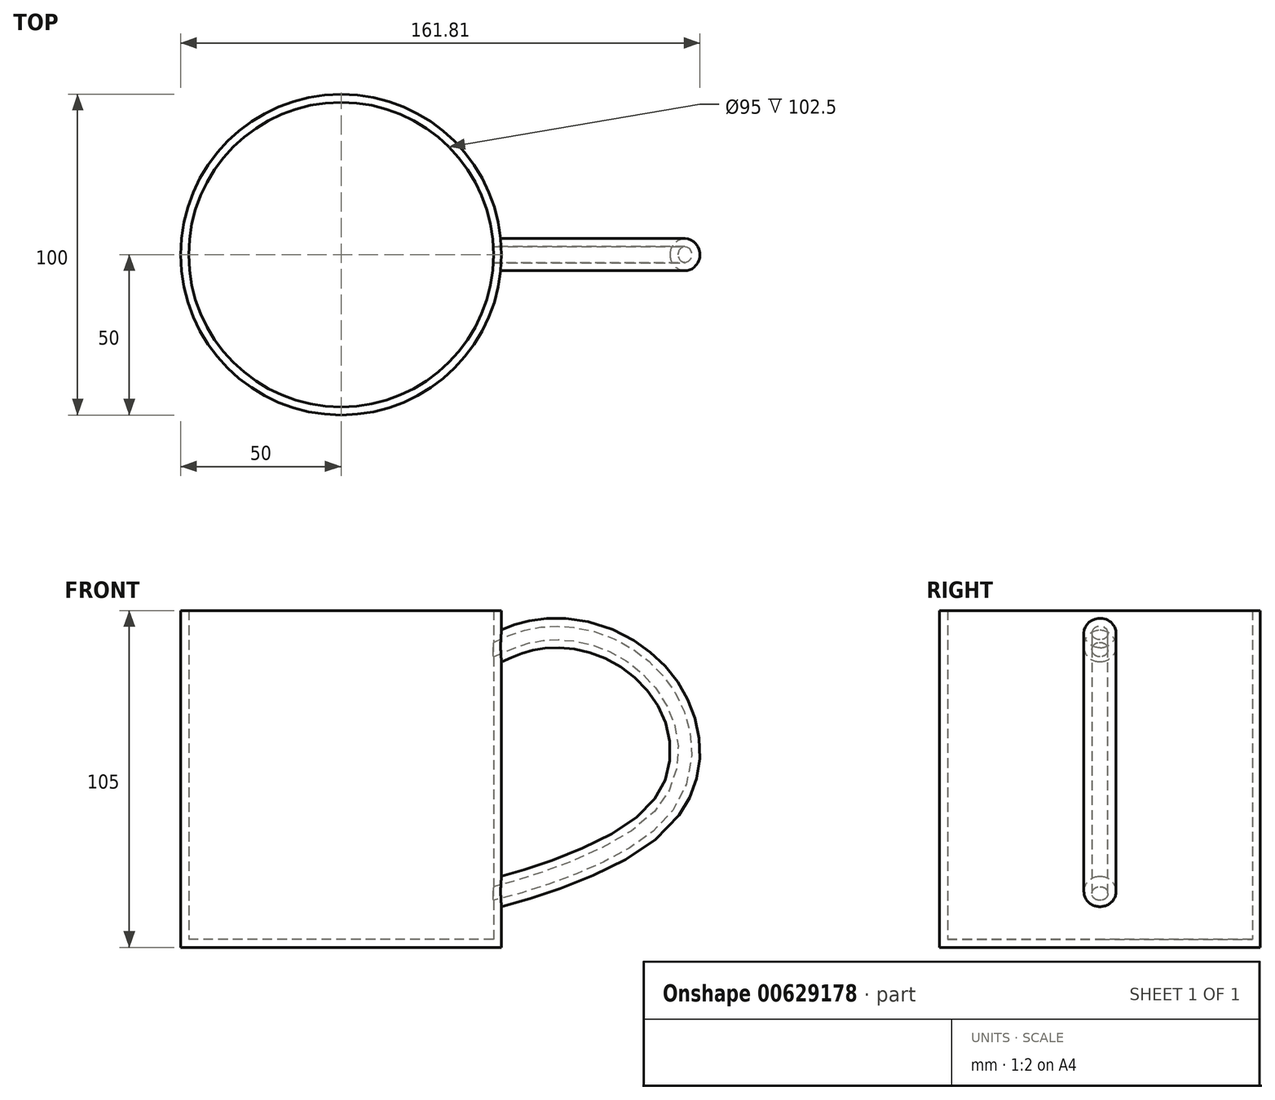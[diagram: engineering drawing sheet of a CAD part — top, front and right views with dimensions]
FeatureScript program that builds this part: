
annotation { "Feature Type Name" : "Feature", "Feature Type Description" : "" }
export const myFeature = defineFeature(function(context is Context, id is Id, definition is map)
    precondition{}
    {
        {
            var Q0;
            Q0=qCreatedBy(makeId("Top.planeOp"),FACE);
            var sketch = newSketch(context, id + "F0", { "sketchPlane" : qUnion([Q0])});
            skCircle(sketch, "E0", {"center": v(0, 0) * mm, "radius": 50 * mm});
            skSolve(sketch);
        }
        {
            var Q0;
            Q0 = qSketchRegion(id + "F0", true);
            extrude(context, id + "F1", {"entities" : qUnion([Q0]), "depth" : 105 * mm, "offsetDistance" : 25 * mm});
        }
        {
            var Q0;
            Q0=qCreatedBy(makeId("Front.planeOp"),FACE);
            var sketch = newSketch(context, id + "F2", { "sketchPlane" : qUnion([Q0])});
            skFitSpline(sketch, "E1", {"points": [v(49.67, 92.28) * mm, v(60.49, 95.98) * mm, v(80.41, 94.27) * mm, v(102.33, 75.2) * mm, v(95.78, 39.62) * mm, v(43.7, 17.42) * mm, v(43.4, 17.42) * mm], "startDerivative": vector(79.98, 35.45) * mm, "endDerivative": vector(-6.49, 2.03) * mm});
            skSolve(sketch);
        }
        {
            var Q0;
            Q0=qCreatedBy(makeId("Right.planeOp"),FACE);
            cPlane(context, id + "F3", {"entities" : qUnion([Q0]), "cplaneType" : CPlaneType.OFFSET, "offset" : 50 * mm, "width" : 150 * mm, "height" : 150 * mm});
        }
        {
            var Q0;
            Q0=qCreatedBy(id+"F3.planeOp",FACE);
            var sketch = newSketch(context, id + "F4", { "sketchPlane" : qUnion([Q0])});
            skCircle(sketch, "E2", {"center": v(0, 93.97) * mm, "radius": 5 * mm});
            skSolve(sketch);
        }
        {
            var Q0;
            Q0 = qSketchRegion(id + "F4", true);
            var Q1;
            Q1=sQuery(id+"F2.wireOp",EDGE,"E1");
            sweep(context, id + "F5", {"operationType" : NewBodyOperationType.ADD, "profiles" : qUnion([Q0]), "path" : qUnion([Q1])});
        }
        {
            var Q0;
            Q0=makeQuery(id+"F1.opExtrude","CAP_FACE",FACE,{"disambiguationData":[OSD([sQuery(id+"F0.wireOp",EDGE,"E0")])],"isStart":false});
            shell(context, id + "F6", {"entities" : qUnion([Q0]), "thickness" : 2.5 * mm});
        }
    });
